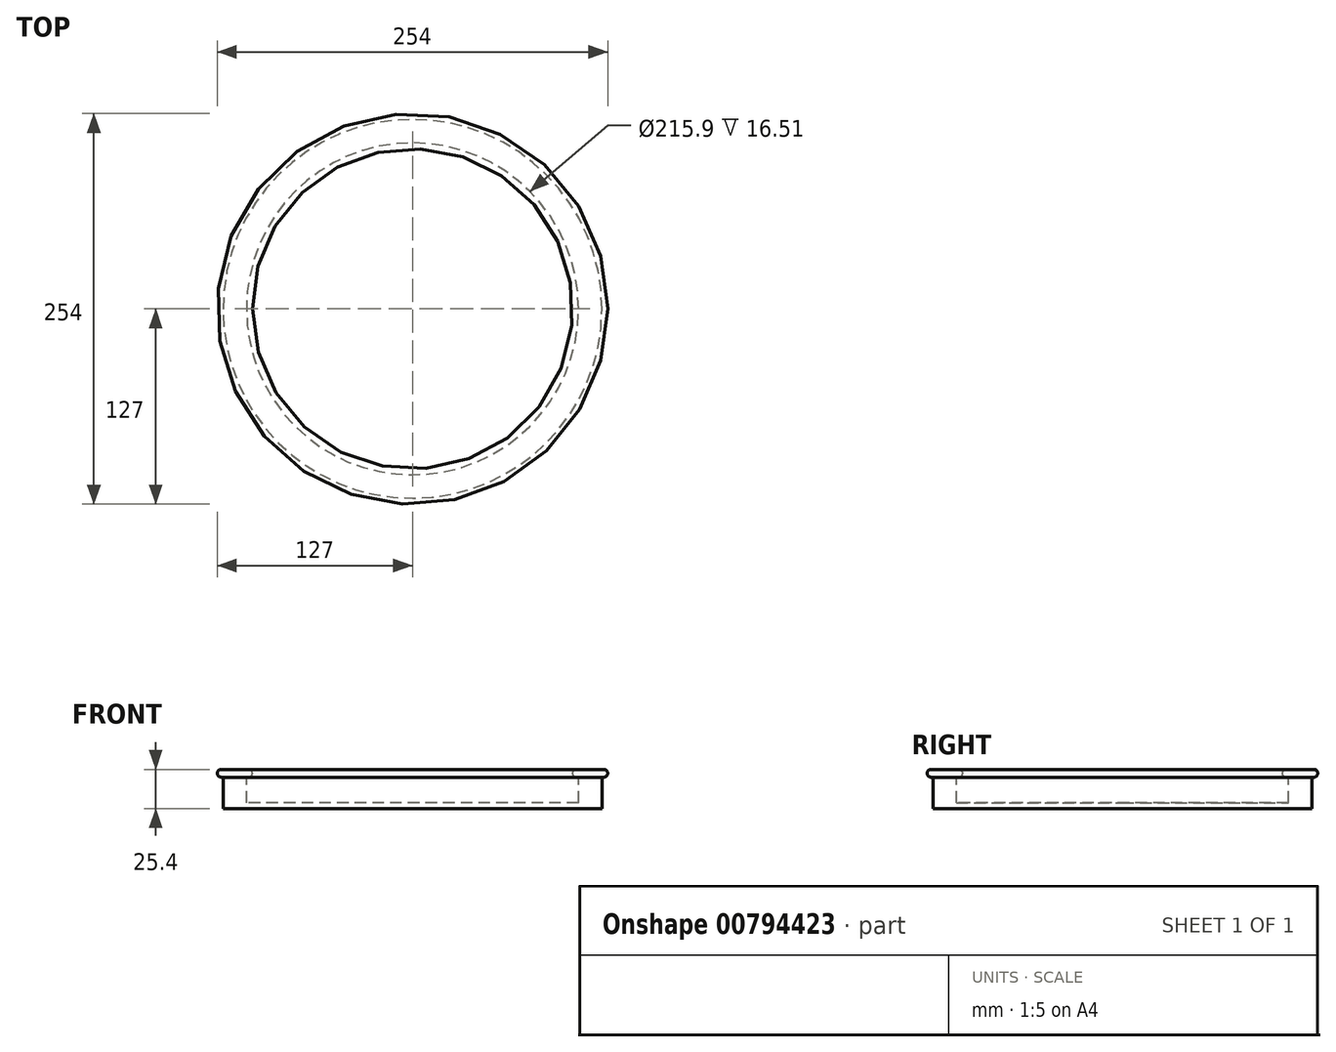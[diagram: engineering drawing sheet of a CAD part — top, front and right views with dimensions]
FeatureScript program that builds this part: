
annotation { "Feature Type Name" : "Feature", "Feature Type Description" : "" }
export const myFeature = defineFeature(function(context is Context, id is Id, definition is map)
    precondition{}
    {
        {
            var Q0;
            Q0=qCreatedBy(makeId("Front.planeOp"),FACE);
            var sketch = newSketch(context, id + "F0", { "sketchPlane" : qUnion([Q0])});
            skLineSegment(sketch, "E0", {"start": v(0, 0) * mm, "end": v(-123.2, 0) * mm});
            skLineSegment(sketch, "E1", {"start": v(-123.2, 0) * mm, "end": v(-123.2, 20.32) * mm});
            skLineSegment(sketch, "E2", {"start": v(-123.2, 20.32) * mm, "end": v(-127, 20.32) * mm});
            skLineSegment(sketch, "E3", {"start": v(-127, 20.32) * mm, "end": v(-127, 25.4) * mm});
            skLineSegment(sketch, "E4", {"start": v(-127, 25.4) * mm, "end": v(-104.14, 25.4) * mm});
            skLineSegment(sketch, "E5", {"start": v(-104.14, 25.4) * mm, "end": v(-104.14, 20.32) * mm});
            skLineSegment(sketch, "E6", {"start": v(-104.14, 20.32) * mm, "end": v(-107.95, 20.32) * mm});
            skLineSegment(sketch, "E7", {"start": v(-107.95, 20.32) * mm, "end": v(-107.95, 3.8) * mm});
            skLineSegment(sketch, "E8", {"start": v(-107.95, 3.81) * mm, "end": v(0, 3.81) * mm});
            skLineSegment(sketch, "E9", {"start": v(0, 3.81) * mm, "end": v(0, 0) * mm});
            skSolve(sketch);
        }
        {
            var Q0;
            Q0 = qSketchRegion(id + "F0", true);
            var Q1;
            Q1=sQuery(id+"F0.wireOp",EDGE,"E9");
            revolve(context, id + "F1", {"surfaceOperationType" : NewSurfaceOperationType.NEW, "entities" : qUnion([Q0]), "axis" : qUnion([Q1]), "revolveType" : RevolveType.FULL});
        }
        {
            var Q0;
            Q0=makeQuery(id+"F1.opRevolve","SWEPT_FACE",FACE,{"disambiguationData":[OSD([sQuery(id+"F0.wireOp",EDGE,"E3")])]});
            var Q1;
            Q1=makeQuery(id+"F1.opRevolve","SWEPT_FACE",FACE,{"disambiguationData":[OSD([sQuery(id+"F0.wireOp",EDGE,"E5")])]});
            fillet(context, id + "F2", {"entities" : qUnion([Q0, Q1]), "radius" : 2.54 * mm, "tangentPropagation" : true, "allowEdgeOverflow" : false});
        }
    });
